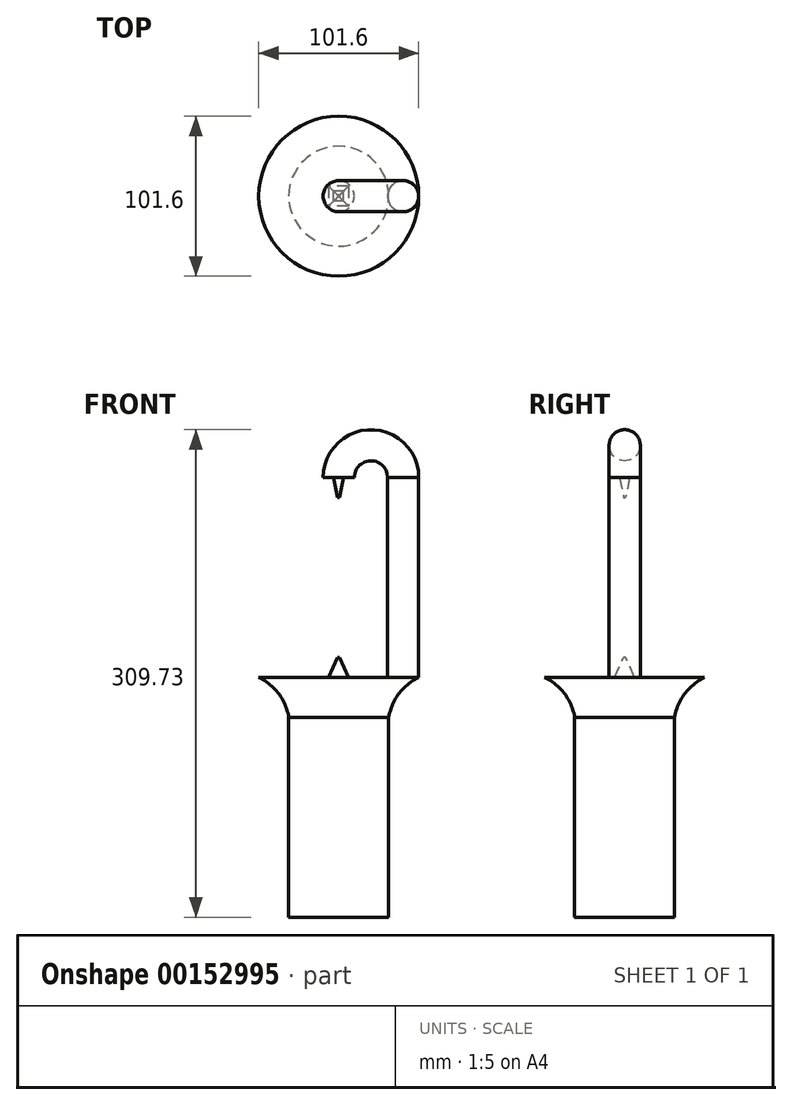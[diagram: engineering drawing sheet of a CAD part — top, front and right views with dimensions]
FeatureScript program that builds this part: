
annotation { "Feature Type Name" : "Feature", "Feature Type Description" : "" }
export const myFeature = defineFeature(function(context is Context, id is Id, definition is map)
    precondition{}
    {
        {
            var Q0;
            Q0=qCreatedBy(makeId("Front.planeOp"),FACE);
            var sketch = newSketch(context, id + "F0", { "sketchPlane" : qUnion([Q0])});
            skLineSegment(sketch, "E0", {"start": v(0, 0) * mm, "end": v(0, 127) * mm});
            skLineSegment(sketch, "E1", {"start": v(0, 127) * mm, "end": v(31.75, 127) * mm});
            skLineSegment(sketch, "E2", {"start": v(31.75, 127) * mm, "end": v(31.75, 0) * mm});
            skLineSegment(sketch, "E3", {"start": v(31.75, 0) * mm, "end": v(0, 0) * mm});
            skLineSegment(sketch, "E4", {"start": v(0, 127) * mm, "end": v(0, 152.4) * mm});
            skLineSegment(sketch, "E5", {"start": v(0, 152.4) * mm, "end": v(50.8, 152.4) * mm});
            skArc(sketch, "E6", {"start": v(50.8, 152.4) * mm, "mid": v(38.2, 142.01) * mm, "end": v(31.75, 127) * mm});
            skSolve(sketch);
        }
        {
            var Q0;
            Q0=makeQuery(id+"F0.imprint","IMPRINT",FACE,{"disambiguationData":[TD([[makeQuery(id+"F0.imprint","IMPRINT",EDGE,{"derivedFrom":sQuery(id+"F0.wireOp",EDGE,"E1")}),1.0]])]});
            var Q1;
            Q1=makeQuery(id+"F0.imprint","IMPRINT",FACE,{"disambiguationData":[TD([[makeQuery(id+"F0.imprint","IMPRINT",EDGE,{"derivedFrom":sQuery(id+"F0.wireOp",EDGE,"E0")}),-1.0]])]});
            var Q2;
            Q2=sQuery(id+"F0.wireOp",EDGE,"E0");
            revolve(context, id + "F1", {"entities" : qUnion([Q0, Q1]), "axis" : qUnion([Q2]), "revolveType" : RevolveType.FULL});
        }
        {
            var Q0;
            Q0=makeQuery(id+"F1.opRevolve","SWEPT_FACE",FACE,{"disambiguationData":[OSD([sQuery(id+"F0.wireOp",EDGE,"E5")])]});
            var sketch = newSketch(context, id + "F2", { "sketchPlane" : qUnion([Q0])});
            skCircle(sketch, "E7", {"center": v(40.9, 0) * mm, "radius": 9.9 * mm});
            skSolve(sketch);
        }
        {
            var Q0;
            Q0=makeQuery(id+"F2.imprint","IMPRINT",FACE,{"disambiguationData":[TD([[makeQuery(id+"F2.imprint","IMPRINT",EDGE,{"derivedFrom":sQuery(id+"F2.wireOp",EDGE,"E7")}),1.0]])]});
            extrude(context, id + "F3", {"entities" : qUnion([Q0]), "operationType" : NewBodyOperationType.ADD, "depth" : 127 * mm});
        }
        {
            var Q0;
            Q0=makeQuery(id+"F1.opRevolve","SWEPT_FACE",FACE,{"disambiguationData":[OSD([sQuery(id+"F0.wireOp",EDGE,"E5")])]});
            var sketch = newSketch(context, id + "F4", { "sketchPlane" : qUnion([Q0])});
            skLineSegment(sketch, "E8.bottom", {"start": v(6.35, 6.35) * mm, "end": v(-6.35, 6.35) * mm});
            skLineSegment(sketch, "E8.top", {"start": v(6.35, -6.35) * mm, "end": v(-6.35, -6.35) * mm});
            skLineSegment(sketch, "E8.left", {"start": v(6.35, 6.35) * mm, "end": v(6.35, -6.35) * mm});
            skLineSegment(sketch, "E8.right", {"start": v(-6.35, 6.35) * mm, "end": v(-6.35, -6.35) * mm});
            skPoint(sketch, "E8.middle", {"position": v(0, 0) * mm});
            skSolve(sketch);
        }
        {
            var Q0;
            Q0=makeQuery(id+"F4.imprint","IMPRINT",FACE,{"disambiguationData":[TD([[makeQuery(id+"F4.imprint","IMPRINT",EDGE,{"derivedFrom":sQuery(id+"F4.wireOp",EDGE,"E8.bottom")}),1.0]])]});
            cPlane(context, id + "F5", {"entities" : qUnion([Q0]), "cplaneType" : CPlaneType.OFFSET, "offset" : 12.7 * mm, "width" : 152.4 * mm, "height" : 152.4 * mm});
        }
        {
            var Q0;
            Q0=qCreatedBy(id+"F5.planeOp",FACE);
            var sketch = newSketch(context, id + "F6", { "sketchPlane" : qUnion([Q0])});
            skLineSegment(sketch, "E9.bottom", {"start": v(0.64, 0.64) * mm, "end": v(-0.64, 0.64) * mm});
            skLineSegment(sketch, "E9.top", {"start": v(0.64, -0.64) * mm, "end": v(-0.64, -0.64) * mm});
            skLineSegment(sketch, "E9.left", {"start": v(0.64, 0.64) * mm, "end": v(0.64, -0.64) * mm});
            skLineSegment(sketch, "E9.right", {"start": v(-0.64, 0.64) * mm, "end": v(-0.64, -0.64) * mm});
            skPoint(sketch, "E9.middle", {"position": v(0, 0) * mm});
            skSolve(sketch);
        }
        {
            var Q1;
            Q1=makeQuery(id+"F4.imprint","IMPRINT",FACE,{"disambiguationData":[TD([[makeQuery(id+"F4.imprint","IMPRINT",EDGE,{"derivedFrom":sQuery(id+"F4.wireOp",EDGE,"E8.bottom")}),1.0]])]});
            var Q2;
            Q2=makeQuery(id+"F6.imprint","IMPRINT",FACE,{"disambiguationData":[TD([[makeQuery(id+"F6.imprint","IMPRINT",EDGE,{"derivedFrom":sQuery(id+"F6.wireOp",EDGE,"E9.bottom")}),1.0]])]});
            loft(context, id + "F7", {"operationType" : NewBodyOperationType.ADD, "sheetProfilesArray" : [{ "sheetProfileEntities" : qUnion([Q1]) }, { "sheetProfileEntities" : qUnion([Q2]) }]});
        }
        {
            var Q0;
            Q0=makeQuery(id+"F3.opExtrude","CAP_FACE",FACE,{"disambiguationData":[OSD([sQuery(id+"F2.wireOp",EDGE,"E7")])],"isStart":false});
            var sketch = newSketch(context, id + "F8", { "sketchPlane" : qUnion([Q0])});
            skCircle(sketch, "E10", {"center": v(40.9, 0) * mm, "radius": 9.88 * mm});
            skLineSegment(sketch, "E11", {"start": v(40.9, 0) * mm, "end": v(0, 0) * mm, "construction": true});
            skLineSegment(sketch, "E12", {"start": v(20.45, 0) * mm, "end": v(20.45, 21.06) * mm, "construction": true});
            skLineSegment(sketch, "E13", {"start": v(20.45, 21.06) * mm, "end": v(20.45, -17.53) * mm, "construction": true});
            skSolve(sketch);
        }
        {
            var Q0;
            Q0=makeQuery(id+"F8.imprint","IMPRINT",FACE,{"disambiguationData":[TD([[makeQuery(id+"F8.imprint","IMPRINT",EDGE,{"derivedFrom":sQuery(id+"F8.wireOp",EDGE,"E10")}),1.0]])]});
            var Q1;
            Q1=sQuery(id+"F8.wireOp",EDGE,"E13");
            revolve(context, id + "F9", {"operationType" : NewBodyOperationType.ADD, "entities" : qUnion([Q0]), "axis" : qUnion([Q1]), "revolveType" : RevolveType.ONE_DIRECTION, "angle" : 180 * degree});
        }
        {
            var Q0;
            Q0=makeQuery(id+"F9.opRevolve","CAP_FACE",FACE,{"disambiguationData":[OSD([sQuery(id+"F8.wireOp",EDGE,"E10")])],"isStart":false});
            cPlane(context, id + "F10", {"entities" : qUnion([Q0]), "cplaneType" : CPlaneType.OFFSET, "offset" : 12.7 * mm, "width" : 152.4 * mm, "height" : 152.4 * mm});
        }
        {
            var Q0;
            Q0=qCreatedBy(id+"F10.planeOp",FACE);
            var sketch = newSketch(context, id + "F11", { "sketchPlane" : qUnion([Q0])});
            skLineSegment(sketch, "E14.bottom", {"start": v(-0.64, 0.64) * mm, "end": v(0.64, 0.64) * mm});
            skLineSegment(sketch, "E14.top", {"start": v(-0.64, -0.64) * mm, "end": v(0.64, -0.64) * mm});
            skLineSegment(sketch, "E14.left", {"start": v(-0.64, 0.64) * mm, "end": v(-0.64, -0.64) * mm});
            skLineSegment(sketch, "E14.right", {"start": v(0.64, 0.64) * mm, "end": v(0.64, -0.64) * mm});
            skPoint(sketch, "E14.middle", {"position": v(0, 0) * mm});
            skSolve(sketch);
        }
        {
            var Q0;
            Q0=makeQuery(id+"F9.opRevolve","CAP_FACE",FACE,{"disambiguationData":[OSD([sQuery(id+"F8.wireOp",EDGE,"E10")])],"isStart":false});
            var sketch = newSketch(context, id + "F12", { "sketchPlane" : qUnion([Q0])});
            skLineSegment(sketch, "E15.bottom", {"start": v(3.18, 3.18) * mm, "end": v(-3.17, 3.18) * mm});
            skLineSegment(sketch, "E15.top", {"start": v(3.18, -3.17) * mm, "end": v(-3.18, -3.17) * mm});
            skLineSegment(sketch, "E15.left", {"start": v(3.18, 3.18) * mm, "end": v(3.18, -3.17) * mm});
            skLineSegment(sketch, "E15.right", {"start": v(-3.17, 3.18) * mm, "end": v(-3.18, -3.17) * mm});
            skPoint(sketch, "E15.middle", {"position": v(0, 0) * mm});
            skSolve(sketch);
        }
        {
            var Q1;
            Q1 = qSketchRegion(id + "F12", true);
            var Q2;
            Q2=makeQuery(id+"F11.imprint","IMPRINT",FACE,{"disambiguationData":[TD([[makeQuery(id+"F11.imprint","IMPRINT",EDGE,{"derivedFrom":sQuery(id+"F11.wireOp",EDGE,"E14.bottom")}),-1.0]])]});
            loft(context, id + "F13", {"operationType" : NewBodyOperationType.ADD, "sheetProfilesArray" : [{ "sheetProfileEntities" : qUnion([Q1]) }, { "sheetProfileEntities" : qUnion([Q2]) }]});
        }
    });
